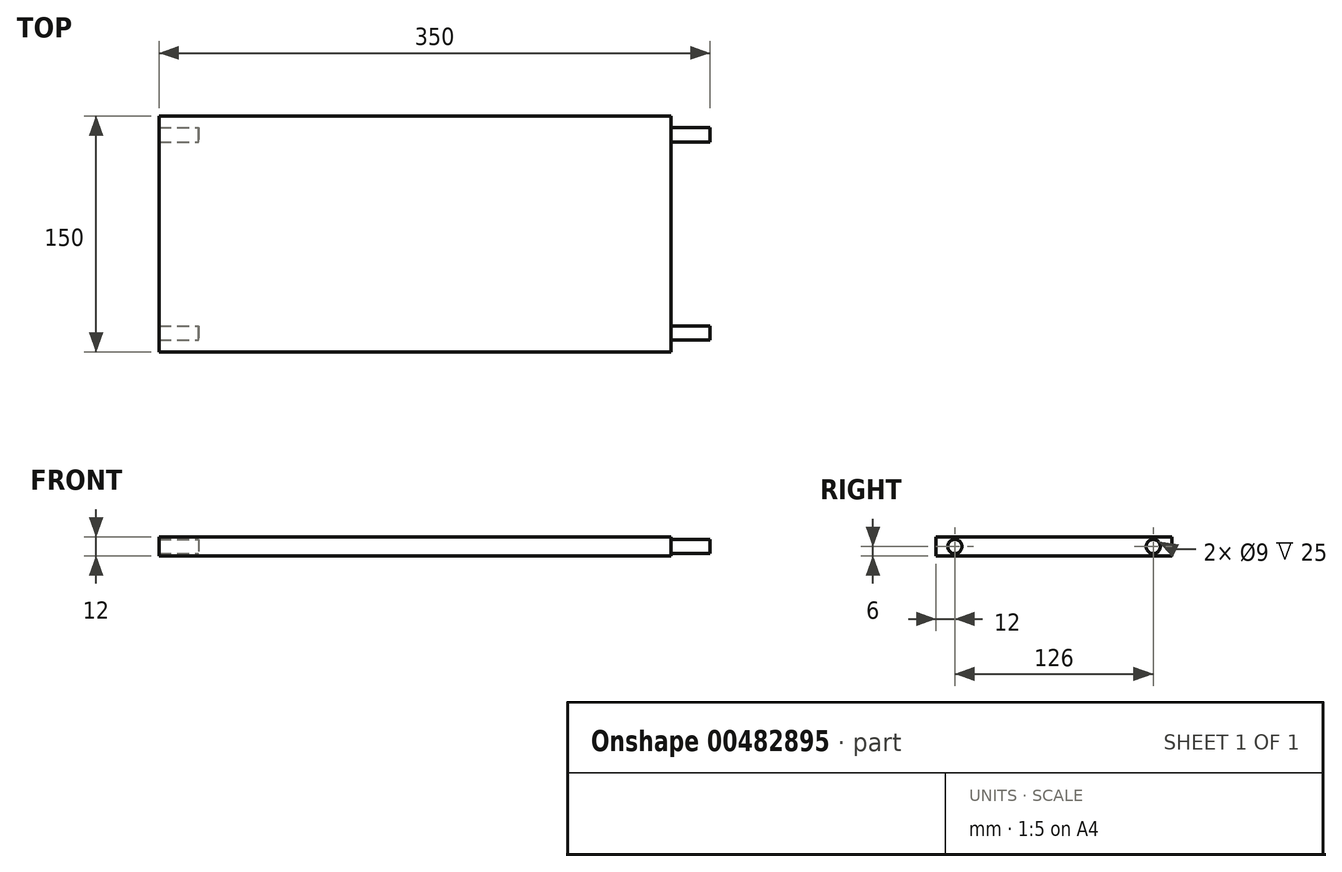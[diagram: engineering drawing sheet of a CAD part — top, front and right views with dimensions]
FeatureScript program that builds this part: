
annotation { "Feature Type Name" : "Feature", "Feature Type Description" : "" }
export const myFeature = defineFeature(function(context is Context, id is Id, definition is map)
    precondition{}
    {
        {
            var Q0;
            Q0=qCreatedBy(makeId("Top.planeOp"),FACE);
            var sketch = newSketch(context, id + "F0", { "sketchPlane" : qUnion([Q0])});
            skLineSegment(sketch, "E0.bottom", {"start": v(150, -75) * mm, "end": v(-150, -75) * mm});
            skLineSegment(sketch, "E0.top", {"start": v(150, 75) * mm, "end": v(-150, 75) * mm});
            skLineSegment(sketch, "E0.left", {"start": v(150, -75) * mm, "end": v(150, 75) * mm});
            skLineSegment(sketch, "E0.right", {"start": v(-150, -75) * mm, "end": v(-150, 75) * mm});
            skPoint(sketch, "E0.middle", {"position": v(0, 0) * mm});
            skSolve(sketch);
        }
        {
            var Q0;
            Q0=makeQuery(id+"F0.imprint","IMPRINT",FACE,{"disambiguationData":[TD([[makeQuery(id+"F0.imprint","IMPRINT",EDGE,{"derivedFrom":sQuery(id+"F0.wireOp",EDGE,"E0.bottom")}),-1.0]])]});
            extrude(context, id + "F1", {"entities" : qUnion([Q0]), "depth" : 12 * mm});
        }
        {
            var Q0;
            Q0=makeQuery(id+"F1.opExtrude","SWEPT_FACE",FACE,{"disambiguationData":[OSD([sQuery(id+"F0.wireOp",EDGE,"E0.left")])]});
            var sketch = newSketch(context, id + "F2", { "sketchPlane" : qUnion([Q0])});
            skCircle(sketch, "E1", {"center": v(-63, 6) * mm, "radius": 4.5 * mm});
            skPoint(sketch, "E1.centerSnap0", {"position": v(-75, 6) * mm});
            skCircle(sketch, "E2", {"center": v(63, 6) * mm, "radius": 4.5 * mm});
            skPoint(sketch, "E2.centerSnap0", {"position": v(75, 6) * mm});
            skSolve(sketch);
        }
        {
            var Q0;
            Q0=makeQuery(id+"F2.imprint","IMPRINT",FACE,{"disambiguationData":[TD([[makeQuery(id+"F2.imprint","IMPRINT",EDGE,{"derivedFrom":sQuery(id+"F2.wireOp",EDGE,"E1")}),1.0]])]});
            var Q1;
            Q1=makeQuery(id+"F2.imprint","IMPRINT",FACE,{"disambiguationData":[TD([[makeQuery(id+"F2.imprint","IMPRINT",EDGE,{"derivedFrom":sQuery(id+"F2.wireOp",EDGE,"E2")}),1.0]])]});
            extrude(context, id + "F3", {"entities" : qUnion([Q0, Q1]), "operationType" : NewBodyOperationType.ADD, "depth" : 25 * mm});
        }
        {
            var Q0;
            Q0=makeQuery(id+"F1.opExtrude","SWEPT_FACE",FACE,{"disambiguationData":[OSD([sQuery(id+"F0.wireOp",EDGE,"E0.right")])]});
            var sketch = newSketch(context, id + "F4", { "sketchPlane" : qUnion([Q0])});
            skCircle(sketch, "E3.0", {"center": v(-63, 6) * mm, "radius": 4.5 * mm});
            skCircle(sketch, "E3.1", {"center": v(63, 6) * mm, "radius": 4.5 * mm});
            skSolve(sketch);
        }
        {
            var Q0;
            Q0=makeQuery(id+"F4.imprint","IMPRINT",FACE,{"disambiguationData":[TD([[makeQuery(id+"F4.imprint","IMPRINT",EDGE,{"derivedFrom":sQuery(id+"F4.wireOp",EDGE,"E3.0")}),-1.0]])]});
            var Q1;
            Q1=makeQuery(id+"F4.imprint","IMPRINT",FACE,{"disambiguationData":[TD([[makeQuery(id+"F4.imprint","IMPRINT",EDGE,{"derivedFrom":sQuery(id+"F4.wireOp",EDGE,"E3.1")}),-1.0]])]});
            extrude(context, id + "F5", {"entities" : qUnion([Q0, Q1]), "operationType" : NewBodyOperationType.ADD, "depth" : 25 * mm});
        }
    });
